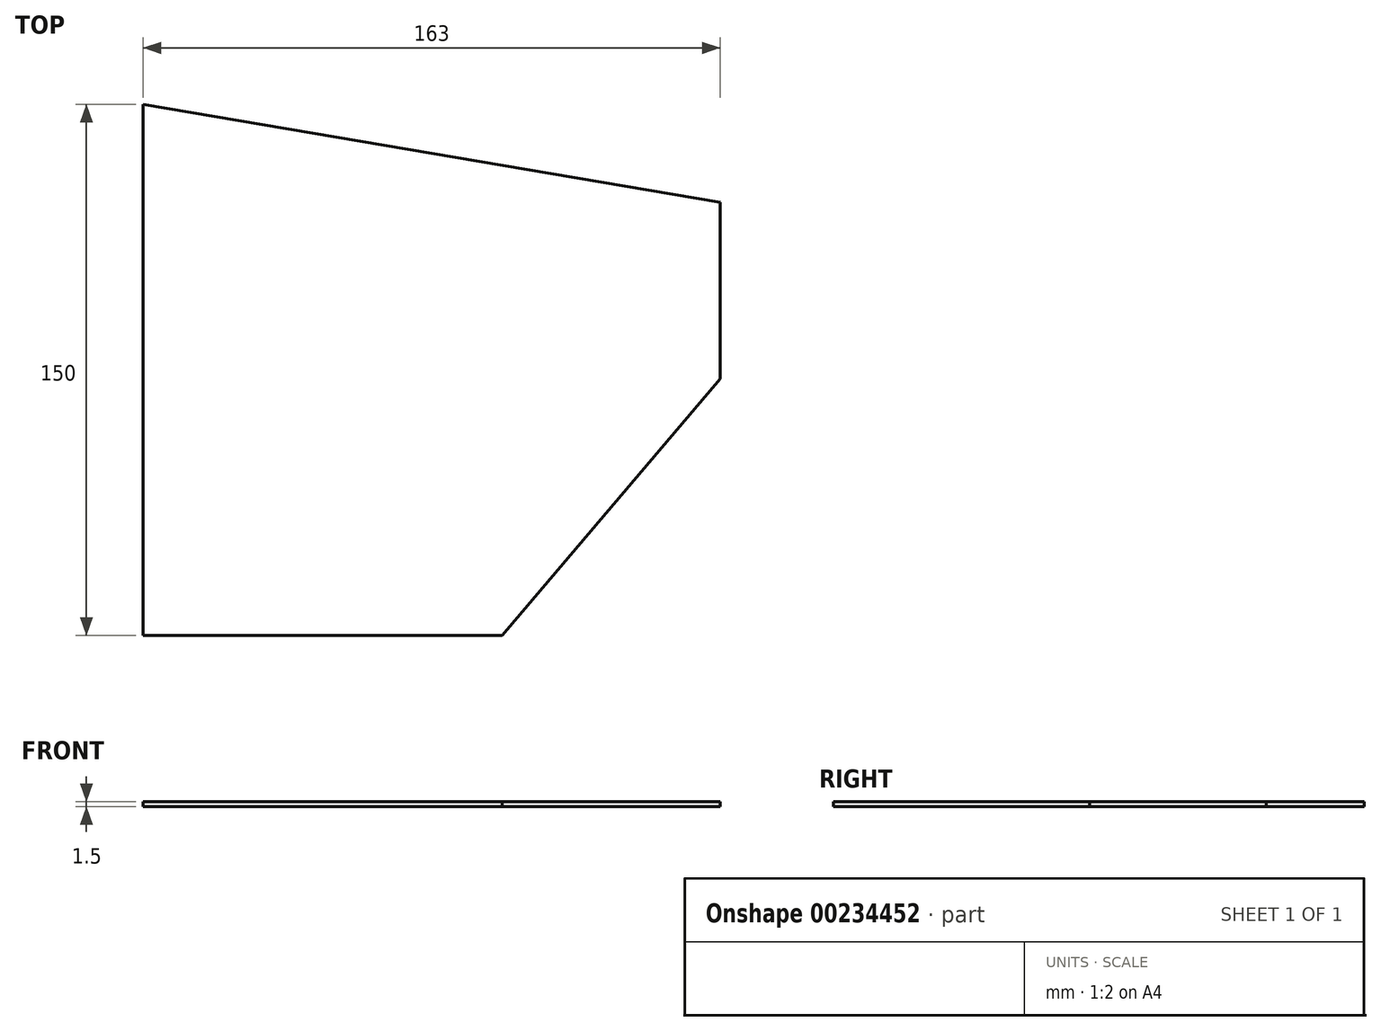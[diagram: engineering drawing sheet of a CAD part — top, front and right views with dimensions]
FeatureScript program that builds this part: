
annotation { "Feature Type Name" : "Feature", "Feature Type Description" : "" }
export const myFeature = defineFeature(function(context is Context, id is Id, definition is map)
    precondition{}
    {
        {
            var Q0;
            Q0=qCreatedBy(makeId("Top.planeOp"),FACE);
            var sketch = newSketch(context, id + "F0", { "sketchPlane" : qUnion([Q0])});
            skLineSegment(sketch, "E0.top", {"start": v(-89.22, -90.2) * mm, "end": v(12.28, -90.2) * mm});
            skLineSegment(sketch, "E0.left", {"start": v(-89.22, 59.8) * mm, "end": v(-89.22, -90.2) * mm});
            skLineSegment(sketch, "E0.right", {"start": v(73.78, 32.21) * mm, "end": v(73.78, -17.79) * mm});
            skLineSegment(sketch, "E1", {"start": v(12.28, -90.2) * mm, "end": v(73.78, -17.79) * mm});
            skLineSegment(sketch, "E2", {"start": v(73.78, -17.79) * mm, "end": v(73.78, 32.21) * mm, "construction": true});
            skLineSegment(sketch, "E3", {"start": v(-89.22, 59.8) * mm, "end": v(73.78, 32.21) * mm});
            skSolve(sketch);
        }
        {
            var Q0;
            Q0 = qSketchRegion(id + "F0", true);
            extrude(context, id + "F1", {"entities" : qUnion([Q0]), "depth" : 1.5 * mm});
        }
    });
